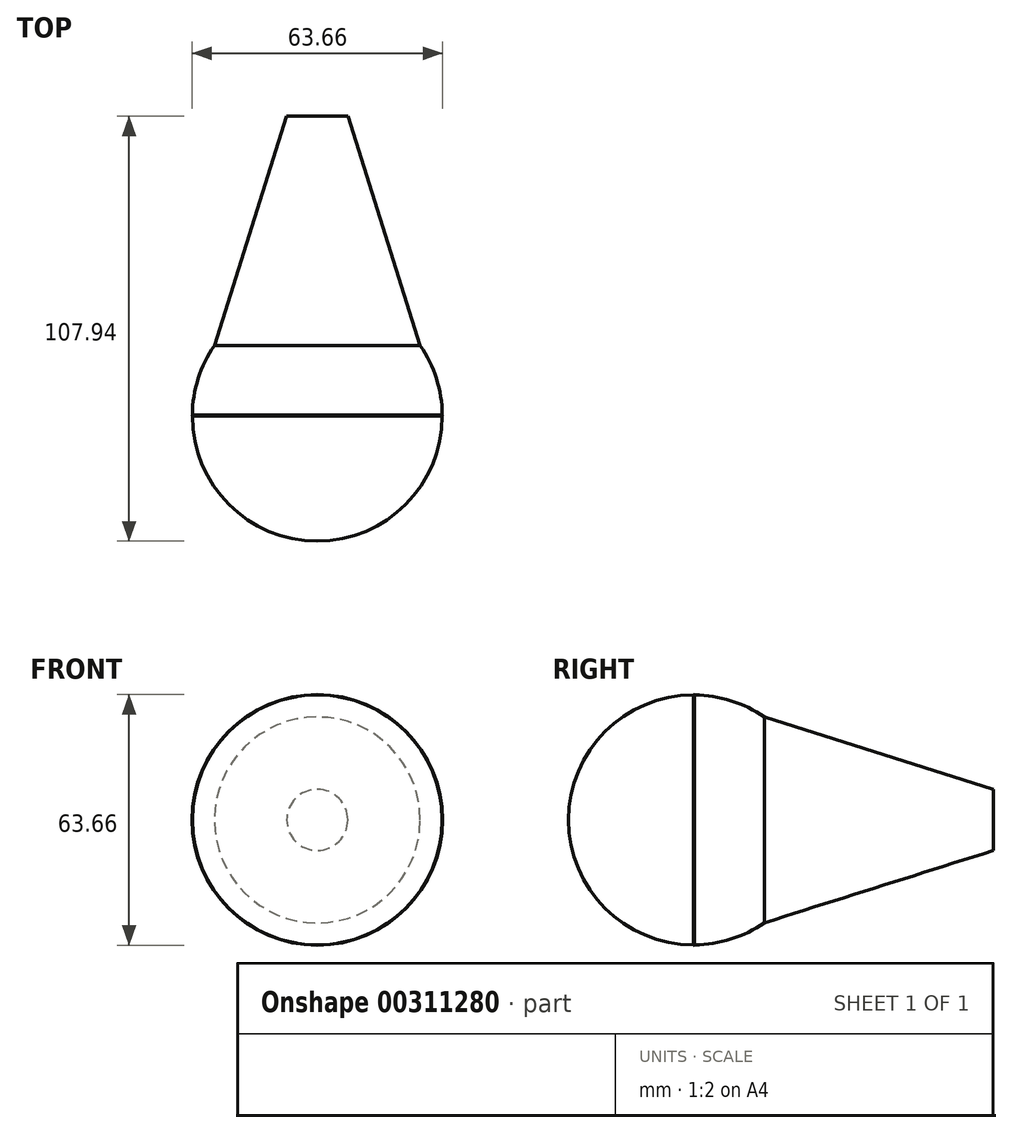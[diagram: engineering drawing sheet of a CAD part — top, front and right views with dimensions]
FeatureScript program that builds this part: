
annotation { "Feature Type Name" : "Feature", "Feature Type Description" : "" }
export const myFeature = defineFeature(function(context is Context, id is Id, definition is map)
    precondition{}
    {
        {
            var Q0;
            Q0=qCreatedBy(makeId("Front.planeOp"),FACE);
            var sketch = newSketch(context, id + "F0", { "sketchPlane" : qUnion([Q0])});
            skCircle(sketch, "E0", {"center": v(0, 0) * mm, "radius": 31.74 * mm});
            skLineSegment(sketch, "E1", {"start": v(0, 66.1) * mm, "end": v(0, -103.4) * mm});
            skSolve(sketch);
        }
        {
            var Q0;
            {var subQ0=sQuery(id+"F0.wireOp",EDGE,"E1");var subQ1=sQuery(id+"F0.wireOp",EDGE,"E0");var subQ2=makeQuery(id+"F0.imprint","INTERSECT",VERTEX,{"disambiguationData":[OD(0.0)],"derivedFrom":[subQ1,subQ0]});Q0=makeQuery(id+"F0.imprint","IMPRINT",FACE,{"disambiguationData":[TD([[makeQuery(id+"F0.imprint","IMPRINT",EDGE,{"disambiguationData":[TD([[subQ2,-1.0]])],"derivedFrom":subQ1}),1.0]])]});}
            var Q1;
            Q1=sQuery(id+"F0.wireOp",EDGE,"E1");
            revolve(context, id + "F1", {"entities" : qUnion([Q0]), "axis" : qUnion([Q1]), "revolveType" : RevolveType.FULL});
        }
        {
            var Q0;
            Q0=qCreatedBy(makeId("Front.planeOp"),FACE);
            var sketch = newSketch(context, id + "F2", { "sketchPlane" : qUnion([Q0])});
            skCircle(sketch, "E2", {"center": v(0, 0) * mm, "radius": 31.83 * mm});
            skSolve(sketch);
        }
        {
            var Q0;
            Q0=qCreatedBy(makeId("Front.planeOp"),FACE);
            cPlane(context, id + "F3", {"entities" : qUnion([Q0]), "cplaneType" : CPlaneType.OFFSET, "offset" : 76.2 * mm, "oppositeDirection" : true, "width" : 152.4 * mm, "height" : 152.4 * mm});
        }
        {
            var Q0;
            Q0=qCreatedBy(id+"F3.planeOp",FACE);
            var sketch = newSketch(context, id + "F4", { "sketchPlane" : qUnion([Q0])});
            skCircle(sketch, "E3", {"center": v(0, 0) * mm, "radius": 7.77 * mm});
            skSolve(sketch);
        }
        {
            var Q1;
            Q1 = qSketchRegion(id + "F2", true);
            var Q2;
            Q2 = qSketchRegion(id + "F4", true);
            loft(context, id + "F5", {"operationType" : NewBodyOperationType.ADD, "sheetProfilesArray" : [{ "sheetProfileEntities" : qUnion([Q1]) }, { "sheetProfileEntities" : qUnion([Q2]) }]});
        }
        {
            var Q0;
            Q0=qCreatedBy(makeId("Front.planeOp"),FACE);
            cPlane(context, id + "F6", {"entities" : qUnion([Q0]), "cplaneType" : CPlaneType.OFFSET, "offset" : 6.35 * mm, "width" : 152.4 * mm, "height" : 152.4 * mm});
        }
    });
